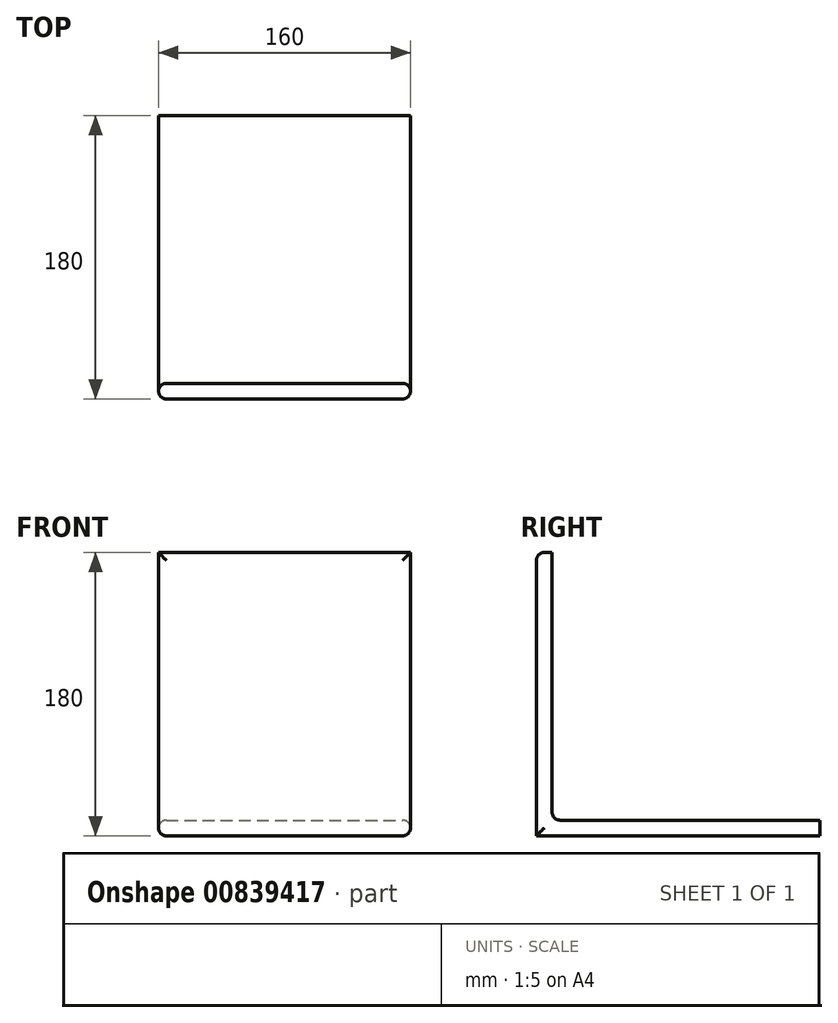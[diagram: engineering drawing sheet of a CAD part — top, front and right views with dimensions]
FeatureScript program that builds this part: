
annotation { "Feature Type Name" : "Feature", "Feature Type Description" : "" }
export const myFeature = defineFeature(function(context is Context, id is Id, definition is map)
    precondition{}
    {
        {
            var Q0;
            Q0=qCreatedBy(makeId("Right.planeOp"),FACE);
            var sketch = newSketch(context, id + "F0", { "sketchPlane" : qUnion([Q0])});
            skLineSegment(sketch, "E0.bottom", {"start": v(-46, 0) * mm, "end": v(134, 0) * mm});
            skLineSegment(sketch, "E0.top", {"start": v(-46, -10) * mm, "end": v(134, -10) * mm});
            skLineSegment(sketch, "E0.left", {"start": v(-46, 0) * mm, "end": v(-46, -10) * mm});
            skLineSegment(sketch, "E0.right", {"start": v(134, 0) * mm, "end": v(134, -10) * mm});
            skLineSegment(sketch, "E1.bottom", {"start": v(-36, -10) * mm, "end": v(-46, -10) * mm});
            skLineSegment(sketch, "E1.top", {"start": v(-36, 170) * mm, "end": v(-46, 170) * mm});
            skLineSegment(sketch, "E1.left", {"start": v(-36, -10) * mm, "end": v(-36, 170) * mm});
            skLineSegment(sketch, "E1.right", {"start": v(-46, -10) * mm, "end": v(-46, 170) * mm});
            skSolve(sketch);
        }
        {
            var Q0;
            Q0 = qSketchRegion(id + "F0", true);
            var Q1;
            {var subQ4=sQuery(id+"F0.wireOp",EDGE,"E0.top");Q1=makeQuery(id+"F0.imprint","IMPRINT",FACE,{"disambiguationData":[TD([[makeQuery(id+"F0.imprint","IMPRINT",EDGE,{"derivedFrom":subQ4}),1.0]])]});}
            extrude(context, id + "F1", {"entities" : qUnion([Q0, Q1]), "oppositeDirection" : true, "depth" : 160 * mm, "offsetDistance" : 25 * mm});
        }
        {
            var Q0;
            Q0=makeQuery(id+"F1.opExtrude","CAP_EDGE",EDGE,{"disambiguationData":[OSD([sQuery(id+"F0.wireOp",EDGE,"E0.bottom")])],"isStart":true});
            var Q1;
            Q1=makeQuery(id+"F1.opExtrude","CAP_EDGE",EDGE,{"disambiguationData":[OSD([sQuery(id+"F0.wireOp",EDGE,"E0.top"),sQuery(id+"F0.wireOp",EDGE,"E1.bottom")])],"isStart":true});
            var Q2;
            Q2=makeQuery(id+"F1.opExtrude","CAP_EDGE",EDGE,{"disambiguationData":[OSD([sQuery(id+"F0.wireOp",EDGE,"E0.bottom")])],"isStart":false});
            var Q3;
            Q3=makeQuery(id+"F1.opExtrude","CAP_EDGE",EDGE,{"disambiguationData":[OSD([sQuery(id+"F0.wireOp",EDGE,"E0.top"),sQuery(id+"F0.wireOp",EDGE,"E1.bottom")])],"isStart":false});
            var Q4;
            Q4=makeQuery(id+"F1.opExtrude","SWEPT_EDGE",EDGE,{"disambiguationData":[OSD([sQuery(id+"F0.wireOp",EDGE,"E0.bottom"),sQuery(id+"F0.wireOp",EDGE,"E1.left")])]});
            var Q5;
            Q5=makeQuery(id+"F1.opExtrude","CAP_EDGE",EDGE,{"disambiguationData":[OSD([sQuery(id+"F0.wireOp",EDGE,"E1.left")])],"isStart":false});
            var Q6;
            Q6=makeQuery(id+"F1.opExtrude","CAP_EDGE",EDGE,{"disambiguationData":[OSD([sQuery(id+"F0.wireOp",EDGE,"E1.right")])],"isStart":false});
            var Q7;
            Q7=makeQuery(id+"F1.opExtrude","CAP_EDGE",EDGE,{"disambiguationData":[OSD([sQuery(id+"F0.wireOp",EDGE,"E1.left")])],"isStart":true});
            var Q8;
            Q8=makeQuery(id+"F1.opExtrude","CAP_EDGE",EDGE,{"disambiguationData":[OSD([sQuery(id+"F0.wireOp",EDGE,"E1.right")])],"isStart":true});
            var Q9;
            Q9=makeQuery(id+"F1.opExtrude","SWEPT_EDGE",EDGE,{"disambiguationData":[OSD([sQuery(id+"F0.wireOp",EDGE,"E1.bottom"),sQuery(id+"F0.wireOp",EDGE,"E1.right")])]});
            fillet(context, id + "F2", {"entities" : qUnion([Q0, Q1, Q2, Q3, Q4, Q5, Q6, Q7, Q8, Q9]), "radius" : 5 * mm, "tangentPropagation" : true, "allowEdgeOverflow" : false});
        }
    });
